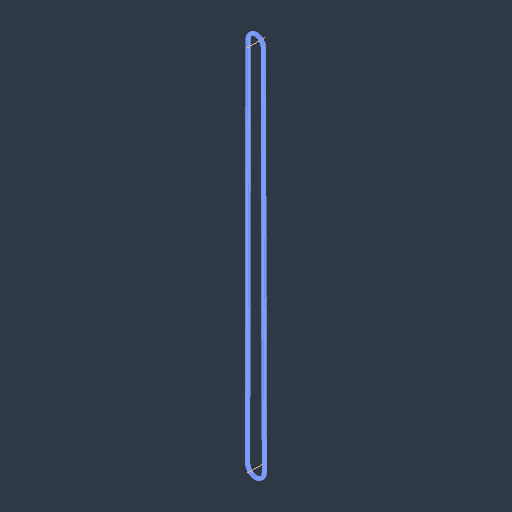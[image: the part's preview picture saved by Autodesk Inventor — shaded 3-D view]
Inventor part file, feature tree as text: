
AUTODESK INVENTOR PART (.ipt)
format: ipt  version: 2024.3 (Build 283343000, 343)  size: 138,752 bytes
history: native  units: mm
features: other x5, plane x2, pattern_linear x1
ambient origin geometry x8: Origin, YZ Plane, XZ Plane, XY Plane, X Axis, Y Axis, Z Axis, Center Point
bodies: Solid1 (feature_tree), Solid (feature_tree)
feature tree (8):
  other  "Work Axis1"
  other  "Work Axis2"
  plane  "Work Plane2"
  plane  "Work Plane3"
  other  "Path"
  other  "Section Plane"
  pattern_linear  "Strand Pattern"  Spacing1=0.0mm  [1 undecoded]
  other  "Section Sketch"
note: 1 required parameter value undecoded (feature->parameter linkage not recoverable at this tier; creation-order binding heuristic only, values carry confidence <= 0.55)
